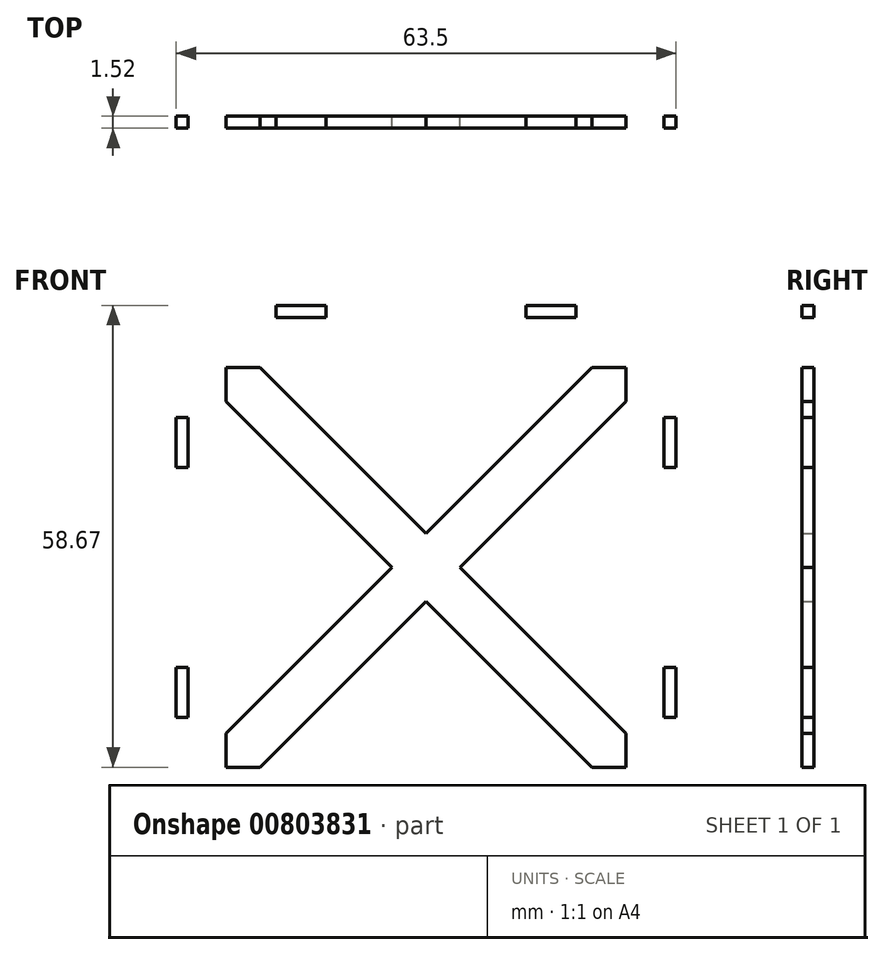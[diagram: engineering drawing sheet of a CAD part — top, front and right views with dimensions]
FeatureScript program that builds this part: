
annotation { "Feature Type Name" : "Feature", "Feature Type Description" : "" }
export const myFeature = defineFeature(function(context is Context, id is Id, definition is map)
    precondition{}
    {
        {
            var Q0;
            Q0=qCreatedBy(makeId("Front.planeOp"),FACE);
            var sketch = newSketch(context, id + "F0", { "sketchPlane" : qUnion([Q0])});
            skLineSegment(sketch, "E0.bottom", {"start": v(31.75, 31.75) * mm, "end": v(-31.75, 31.75) * mm});
            skLineSegment(sketch, "E0.top", {"start": v(31.75, -31.75) * mm, "end": v(-31.75, -31.75) * mm});
            skLineSegment(sketch, "E0.left", {"start": v(31.75, 31.75) * mm, "end": v(31.75, -31.75) * mm});
            skLineSegment(sketch, "E0.right", {"start": v(-31.75, 31.75) * mm, "end": v(-31.75, -31.75) * mm});
            skPoint(sketch, "E0.middle", {"position": v(0, 0) * mm});
            skLineSegment(sketch, "E1.bottom", {"start": v(-19.05, -31.75) * mm, "end": v(-12.7, -31.75) * mm});
            skLineSegment(sketch, "E1.top", {"start": v(-19.05, -33.27) * mm, "end": v(-12.7, -33.27) * mm});
            skLineSegment(sketch, "E1.left", {"start": v(-19.05, -31.75) * mm, "end": v(-19.05, -33.27) * mm});
            skLineSegment(sketch, "E1.right", {"start": v(-12.7, -31.75) * mm, "end": v(-12.7, -33.27) * mm});
            skPoint(sketch, "E2", {"position": v(-15.88, -31.75) * mm});
            skLineSegment(sketch, "E3.MirrorCS", {"start": v(19.05, -31.75) * mm, "end": v(12.7, -31.75) * mm});
            skPoint(sketch, "E4.MirrorP", {"position": v(15.88, -31.75) * mm});
            skLineSegment(sketch, "E5.MirrorCS", {"start": v(19.05, -33.27) * mm, "end": v(12.7, -33.27) * mm});
            skLineSegment(sketch, "E6.MirrorCS", {"start": v(12.7, -31.75) * mm, "end": v(12.7, -33.27) * mm});
            skLineSegment(sketch, "E7.MirrorCS", {"start": v(19.05, -31.75) * mm, "end": v(19.05, -33.27) * mm});
            skLineSegment(sketch, "E8.bottom", {"start": v(-31.75, -19.05) * mm, "end": v(-30.23, -19.05) * mm});
            skLineSegment(sketch, "E8.top", {"start": v(-31.75, -12.7) * mm, "end": v(-30.23, -12.7) * mm});
            skLineSegment(sketch, "E8.left", {"start": v(-31.75, -19.05) * mm, "end": v(-31.75, -12.7) * mm});
            skLineSegment(sketch, "E8.right", {"start": v(-30.23, -19.05) * mm, "end": v(-30.23, -12.7) * mm});
            skPoint(sketch, "E9", {"position": v(-31.75, -15.88) * mm});
            skLineSegment(sketch, "E10.MirrorCS", {"start": v(-31.75, 19.05) * mm, "end": v(-30.23, 19.05) * mm});
            skPoint(sketch, "E11.MirrorP", {"position": v(-31.75, 15.88) * mm});
            skLineSegment(sketch, "E12.MirrorCS", {"start": v(-31.75, 12.7) * mm, "end": v(-30.23, 12.7) * mm});
            skLineSegment(sketch, "E13.MirrorCS", {"start": v(-31.75, 19.05) * mm, "end": v(-31.75, 12.7) * mm});
            skLineSegment(sketch, "E14.MirrorCS", {"start": v(-30.23, 19.05) * mm, "end": v(-30.23, 12.7) * mm});
            skLineSegment(sketch, "E15.MirrorCS", {"start": v(31.75, 19.05) * mm, "end": v(30.23, 19.05) * mm});
            skLineSegment(sketch, "E16.MirrorCS", {"start": v(31.75, -19.05) * mm, "end": v(30.23, -19.05) * mm});
            skLineSegment(sketch, "E17.MirrorCS", {"start": v(31.75, -12.7) * mm, "end": v(30.23, -12.7) * mm});
            skLineSegment(sketch, "E18.MirrorCS", {"start": v(31.75, 12.7) * mm, "end": v(30.23, 12.7) * mm});
            skLineSegment(sketch, "E19.MirrorCS", {"start": v(30.23, 19.05) * mm, "end": v(30.23, 12.7) * mm});
            skLineSegment(sketch, "E20.MirrorCS", {"start": v(30.23, -19.05) * mm, "end": v(30.23, -12.7) * mm});
            skLineSegment(sketch, "E21.MirrorCS", {"start": v(31.75, 19.05) * mm, "end": v(31.75, 12.7) * mm});
            skLineSegment(sketch, "E22.MirrorCS", {"start": v(31.75, -19.05) * mm, "end": v(31.75, -12.7) * mm});
            skPoint(sketch, "E23.MirrorP", {"position": v(31.75, 15.88) * mm});
            skPoint(sketch, "E24.MirrorP", {"position": v(31.75, -15.88) * mm});
            skLineSegment(sketch, "E25.0", {"start": v(-30.23, 31.75) * mm, "end": v(-30.23, -31.75) * mm});
            skLineSegment(sketch, "E26.MirrorCS", {"start": v(30.23, 31.75) * mm, "end": v(30.23, -31.75) * mm});
            skLineSegment(sketch, "E27.bottom", {"start": v(25.4, 25.4) * mm, "end": v(-25.4, 25.4) * mm});
            skLineSegment(sketch, "E27.top", {"start": v(25.4, -25.4) * mm, "end": v(-25.4, -25.4) * mm});
            skLineSegment(sketch, "E27.left", {"start": v(25.4, 25.4) * mm, "end": v(25.4, -25.4) * mm});
            skLineSegment(sketch, "E27.right", {"start": v(-25.4, 25.4) * mm, "end": v(-25.4, -25.4) * mm});
            skLineSegment(sketch, "E28", {"start": v(-25.4, -25.4) * mm, "end": v(25.4, 25.4) * mm, "construction": true});
            skLineSegment(sketch, "E29", {"start": v(-25.4, 25.4) * mm, "end": v(25.4, -25.4) * mm, "construction": true});
            skLineSegment(sketch, "E30.0", {"start": v(-27.56, 23.24) * mm, "end": v(23.24, -27.56) * mm});
            skLineSegment(sketch, "E31.0", {"start": v(-23.24, 27.56) * mm, "end": v(27.56, -23.24) * mm});
            skLineSegment(sketch, "E32.0", {"start": v(-23.24, -27.56) * mm, "end": v(27.56, 23.24) * mm});
            skLineSegment(sketch, "E33.0", {"start": v(-27.56, -23.24) * mm, "end": v(23.24, 27.56) * mm});
            skLineSegment(sketch, "E34.MirrorCS", {"start": v(-12.7, 31.75) * mm, "end": v(-12.7, 33.27) * mm});
            skLineSegment(sketch, "E35.MirrorCS", {"start": v(19.05, 31.75) * mm, "end": v(19.05, 33.27) * mm});
            skLineSegment(sketch, "E36.MirrorCS", {"start": v(12.7, 31.75) * mm, "end": v(12.7, 33.27) * mm});
            skLineSegment(sketch, "E37.MirrorCS", {"start": v(-19.05, 31.75) * mm, "end": v(-19.05, 33.27) * mm});
            skPoint(sketch, "E38.MirrorP", {"position": v(-15.88, 31.75) * mm});
            skLineSegment(sketch, "E39.MirrorCS", {"start": v(19.05, 31.75) * mm, "end": v(12.7, 31.75) * mm});
            skLineSegment(sketch, "E40.MirrorCS", {"start": v(19.05, 33.27) * mm, "end": v(12.7, 33.27) * mm});
            skPoint(sketch, "E41.MirrorP", {"position": v(15.88, 31.75) * mm});
            skLineSegment(sketch, "E42.MirrorCS", {"start": v(-19.05, 33.27) * mm, "end": v(-12.7, 33.27) * mm});
            skLineSegment(sketch, "E43.MirrorCS", {"start": v(-19.05, 31.75) * mm, "end": v(-12.7, 31.75) * mm});
            skSolve(sketch);
        }
        {
            var Q0;
            {var subQ8=sQuery(id+"F0.wireOp",EDGE,"E1.bottom");Q0=makeQuery(id+"F0.imprint","IMPRINT",FACE,{"disambiguationData":[TD([[makeQuery(id+"F0.imprint","IMPRINT",EDGE,{"derivedFrom":subQ8}),1.0]])]});}
            var Q1;
            {var subQ0=sQuery(id+"F0.wireOp",EDGE,"E10.MirrorCS");Q1=makeQuery(id+"F0.imprint","IMPRINT",FACE,{"disambiguationData":[TD([[makeQuery(id+"F0.imprint","IMPRINT",EDGE,{"derivedFrom":subQ0}),-1.0]])]});}
            var Q2;
            {var subQ0=sQuery(id+"F0.wireOp",EDGE,"E8.bottom");Q2=makeQuery(id+"F0.imprint","IMPRINT",FACE,{"disambiguationData":[TD([[makeQuery(id+"F0.imprint","IMPRINT",EDGE,{"derivedFrom":subQ0}),1.0]])]});}
            var Q3;
            {var subQ0=sQuery(id+"F0.wireOp",EDGE,"E16.MirrorCS");Q3=makeQuery(id+"F0.imprint","IMPRINT",FACE,{"disambiguationData":[TD([[makeQuery(id+"F0.imprint","IMPRINT",EDGE,{"derivedFrom":subQ0}),-1.0]])]});}
            var Q4;
            {var subQ0=sQuery(id+"F0.wireOp",EDGE,"E15.MirrorCS");Q4=makeQuery(id+"F0.imprint","IMPRINT",FACE,{"disambiguationData":[TD([[makeQuery(id+"F0.imprint","IMPRINT",EDGE,{"derivedFrom":subQ0}),1.0]])]});}
            var Q5;
            Q5=makeQuery(id+"F0.imprint","IMPRINT",FACE,{"disambiguationData":[TD([[makeQuery(id+"F0.imprint","IMPRINT",EDGE,{"derivedFrom":sQuery(id+"F0.wireOp",EDGE,"E1.bottom")}),-1.0]])]});
            var Q6;
            Q6=makeQuery(id+"F0.imprint","IMPRINT",FACE,{"disambiguationData":[TD([[makeQuery(id+"F0.imprint","IMPRINT",EDGE,{"derivedFrom":sQuery(id+"F0.wireOp",EDGE,"E3.MirrorCS")}),1.0]])]});
            var Q7;
            {var subQ1=sQuery(id+"F0.wireOp",EDGE,"E27.bottom");var subQ5=sQuery(id+"F0.wireOp",EDGE,"E27.right");var subQ6=makeQuery(id+"F0.imprint","INTERSECT",VERTEX,{"derivedFrom":[subQ1,subQ5]});Q7=makeQuery(id+"F0.imprint","IMPRINT",FACE,{"disambiguationData":[TD([[makeQuery(id+"F0.imprint","IMPRINT",EDGE,{"disambiguationData":[TD([[subQ6,1.0]])],"derivedFrom":subQ1}),1.0]])]});}
            var Q8;
            {var subQ5=sQuery(id+"F0.wireOp",EDGE,"E27.left");var subQ6=sQuery(id+"F0.wireOp",EDGE,"E27.bottom");var subQ7=makeQuery(id+"F0.imprint","INTERSECT",VERTEX,{"derivedFrom":[subQ6,subQ5]});Q8=makeQuery(id+"F0.imprint","IMPRINT",FACE,{"disambiguationData":[TD([[makeQuery(id+"F0.imprint","IMPRINT",EDGE,{"disambiguationData":[TD([[subQ7,-1.0]])],"derivedFrom":subQ6}),1.0]])]});}
            var Q9;
            {var subQ1=sQuery(id+"F0.wireOp",EDGE,"E27.left");var subQ6=sQuery(id+"F0.wireOp",EDGE,"E27.top");var subQ9=makeQuery(id+"F0.imprint","INTERSECT",VERTEX,{"derivedFrom":[subQ6,subQ1]});Q9=makeQuery(id+"F0.imprint","IMPRINT",FACE,{"disambiguationData":[TD([[makeQuery(id+"F0.imprint","IMPRINT",EDGE,{"disambiguationData":[TD([[subQ9,-1.0]])],"derivedFrom":subQ6}),-1.0]])]});}
            var Q10;
            {var subQ1=sQuery(id+"F0.wireOp",EDGE,"E27.top");var subQ7=sQuery(id+"F0.wireOp",EDGE,"E27.right");var subQ8=makeQuery(id+"F0.imprint","INTERSECT",VERTEX,{"derivedFrom":[subQ1,subQ7]});Q10=makeQuery(id+"F0.imprint","IMPRINT",FACE,{"disambiguationData":[TD([[makeQuery(id+"F0.imprint","IMPRINT",EDGE,{"disambiguationData":[TD([[subQ8,1.0]])],"derivedFrom":subQ1}),-1.0]])]});}
            var Q11;
            {var subQ0=sQuery(id+"F0.wireOp",EDGE,"E33.0");var subQ1=sQuery(id+"F0.wireOp",EDGE,"E30.0");var subQ2=makeQuery(id+"F0.imprint","INTERSECT",VERTEX,{"derivedFrom":[subQ1,subQ0]});Q11=makeQuery(id+"F0.imprint","IMPRINT",FACE,{"disambiguationData":[TD([[makeQuery(id+"F0.imprint","IMPRINT",EDGE,{"disambiguationData":[TD([[subQ2,-1.0]])],"derivedFrom":subQ1}),1.0]])]});}
            var Q12;
            Q12=makeQuery(id+"F0.imprint","IMPRINT",FACE,{"disambiguationData":[TD([[makeQuery(id+"F0.imprint","IMPRINT",EDGE,{"derivedFrom":sQuery(id+"F0.wireOp",EDGE,"E34.MirrorCS")}),1.0]])]});
            var Q13;
            Q13=makeQuery(id+"F0.imprint","IMPRINT",FACE,{"disambiguationData":[TD([[makeQuery(id+"F0.imprint","IMPRINT",EDGE,{"derivedFrom":sQuery(id+"F0.wireOp",EDGE,"E35.MirrorCS")}),1.0]])]});
            extrude(context, id + "F1", {"entities" : qUnion([Q0, Q1, Q2, Q3, Q4, Q5, Q6, Q7, Q8, Q9, Q10, Q11, Q12, Q13]), "depth" : 1.52 * mm, "offsetDistance" : 25.4 * mm});
        }
    });
